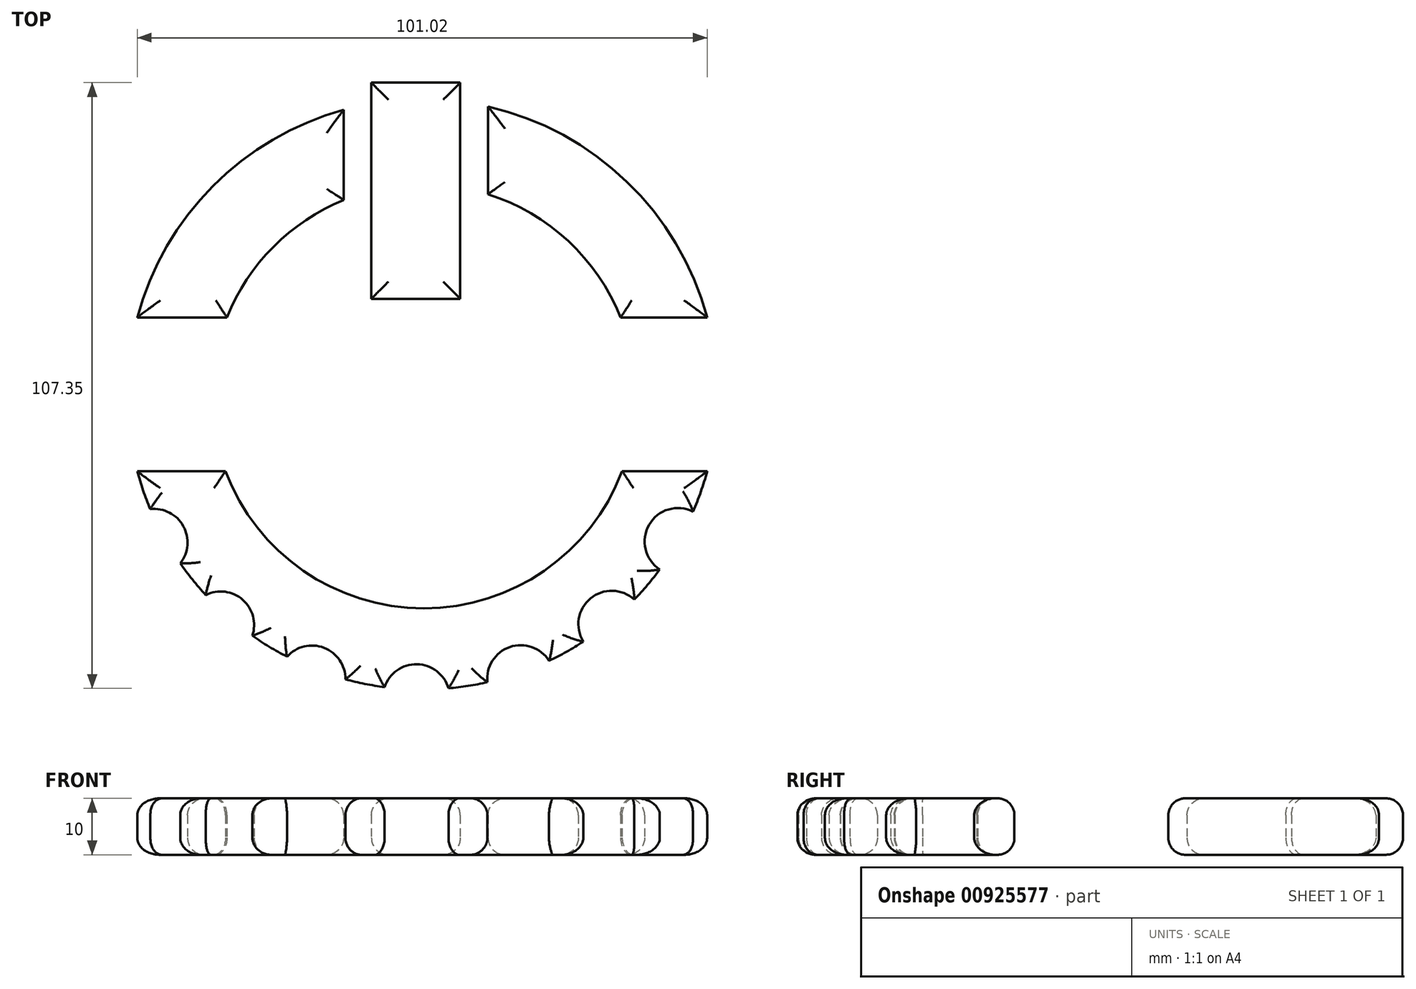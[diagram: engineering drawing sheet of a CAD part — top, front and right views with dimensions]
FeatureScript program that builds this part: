
annotation { "Feature Type Name" : "Feature", "Feature Type Description" : "" }
export const myFeature = defineFeature(function(context is Context, id is Id, definition is map)
    precondition{}
    {
        {
            var Q0;
            Q0=qCreatedBy(makeId("Top.planeOp"),FACE);
            var sketch = newSketch(context, id + "F0", { "sketchPlane" : qUnion([Q0])});
            skArc(sketch, "E0", {"start": v(-12.8, 35.35) * mm, "mid": v(-25.25, 27.04) * mm, "end": v(-33.48, 14.53) * mm});
            skArc(sketch, "E1", {"start": v(-12.8, 51.32) * mm, "mid": v(-35.97, 37.78) * mm, "end": v(-49.38, 14.53) * mm});
            skLineSegment(sketch, "E2.bottom", {"start": v(7.88, 17.84) * mm, "end": v(-7.88, 17.84) * mm});
            skLineSegment(sketch, "E2.top", {"start": v(7.88, 56.13) * mm, "end": v(-7.88, 56.13) * mm});
            skLineSegment(sketch, "E2.left", {"start": v(7.88, 17.84) * mm, "end": v(7.88, 56.13) * mm});
            skLineSegment(sketch, "E2.right", {"start": v(-7.88, 17.84) * mm, "end": v(-7.88, 56.13) * mm});
            skPoint(sketch, "E2.middle", {"position": v(0, 36.99) * mm});
            skLineSegment(sketch, "E3.bottom", {"start": v(51.64, -12.75) * mm, "end": v(36.57, -12.75) * mm});
            skLineSegment(sketch, "E3.top", {"start": v(51.64, 14.53) * mm, "end": v(36.3, 14.53) * mm});
            skArc(sketch, "E4", {"start": v(49.15, -19.89) * mm, "mid": v(41.35, -22.23) * mm, "end": v(43.25, -30.15) * mm});
            skPoint(sketch, "E5.orphan", {"position": v(12.8, 62.31) * mm});
            skPoint(sketch, "E6.orphan", {"position": v(-12.8, 61.71) * mm});
            skLineSegment(sketch, "E7.trimOffspring", {"start": v(12.8, 36.37) * mm, "end": v(12.8, 51.9) * mm});
            skLineSegment(sketch, "E8.trimOffspring", {"start": v(-12.8, 35.35) * mm, "end": v(-12.8, 51.32) * mm});
            skArc(sketch, "E9.trimOffspring", {"start": v(-49.38, -12.75) * mm, "mid": v(-48.34, -16.14) * mm, "end": v(-47.07, -19.46) * mm});
            skArc(sketch, "E10.trimOffspring", {"start": v(-33.75, -12.75) * mm, "mid": v(1.41, -37.04) * mm, "end": v(36.57, -12.75) * mm});
            skLineSegment(sketch, "E11.trimOffspring", {"start": v(-33.48, 14.53) * mm, "end": v(-49.38, 14.53) * mm});
            skPoint(sketch, "E3.right.end.orphan", {"position": v(-91.26, 14.53) * mm});
            skPoint(sketch, "E12.orphan", {"position": v(-55.52, -12.75) * mm});
            skLineSegment(sketch, "E13.trimOffspring", {"start": v(-33.75, -12.75) * mm, "end": v(-49.38, -12.75) * mm});
            skArc(sketch, "E14.trimOffspring", {"start": v(36.3, 14.53) * mm, "mid": v(27, 28.09) * mm, "end": v(12.8, 36.37) * mm});
            skPoint(sketch, "E15.left.start.orphan", {"position": v(12.8, 12.26) * mm});
            skPoint(sketch, "E15.right.start.orphan", {"position": v(-12.8, 11.66) * mm});
            skArc(sketch, "E16.trimOffspring", {"start": v(51.64, 14.53) * mm, "mid": v(37.4, 38.6) * mm, "end": v(12.8, 51.9) * mm});
            skPoint(sketch, "E17.orphan", {"position": v(93.52, -12.75) * mm});
            skArc(sketch, "E18.1.0", {"start": v(38.73, -35.48) * mm, "mid": v(30.97, -35.29) * mm, "end": v(29.68, -42.95) * mm});
            skArc(sketch, "E18.2.0", {"start": v(23.61, -46.35) * mm, "mid": v(16.65, -43.9) * mm, "end": v(12.7, -50.13) * mm});
            skArc(sketch, "E18.3.0", {"start": v(5.79, -51.22) * mm, "mid": v(0.2, -46.95) * mm, "end": v(-5.53, -51) * mm});
            skArc(sketch, "E18.4.0", {"start": v(-12.49, -49.62) * mm, "mid": v(-16.27, -44.03) * mm, "end": v(-22.83, -45.61) * mm});
            skArc(sketch, "E18.5.0", {"start": v(-28.98, -41.9) * mm, "mid": v(-30.7, -35.52) * mm, "end": v(-37.23, -34.68) * mm});
            skArc(sketch, "E18.6.0", {"start": v(-41.77, -29.05) * mm, "mid": v(-41.2, -22.48) * mm, "end": v(-47.07, -19.46) * mm});
            skPoint(sketch, "E18.center", {"position": v(0, 0) * mm});
            skLineSegment(sketch, "E18.anchor1", {"start": v(0, 0) * mm, "end": v(46.49, -25.18) * mm, "construction": true});
            skLineSegment(sketch, "E18.anchor2", {"start": v(0, 0) * mm, "end": v(-41.2, -22.5) * mm, "construction": true});
            skLineSegment(sketch, "E19.trimOffspring", {"start": v(-44.67, -24.4) * mm, "end": v(-46.4, -25.35) * mm, "construction": true});
            skArc(sketch, "E20.trimOffspring", {"start": v(-41.77, -29.05) * mm, "mid": v(-39.6, -31.94) * mm, "end": v(-37.23, -34.68) * mm});
            skArc(sketch, "E21.trimOffspring", {"start": v(-28.98, -41.9) * mm, "mid": v(-25.97, -43.86) * mm, "end": v(-22.83, -45.61) * mm});
            skArc(sketch, "E22.trimOffspring", {"start": v(-12.49, -49.62) * mm, "mid": v(-9.03, -50.43) * mm, "end": v(-5.53, -51) * mm});
            skArc(sketch, "E23.trimOffspring", {"start": v(5.79, -51.22) * mm, "mid": v(9.26, -50.79) * mm, "end": v(12.7, -50.13) * mm});
            skArc(sketch, "E24.trimOffspring", {"start": v(23.61, -46.35) * mm, "mid": v(26.7, -44.75) * mm, "end": v(29.68, -42.95) * mm});
            skArc(sketch, "E25.trimOffspring", {"start": v(38.73, -35.48) * mm, "mid": v(41.08, -32.9) * mm, "end": v(43.25, -30.15) * mm});
            skArc(sketch, "E26.trimOffspring", {"start": v(49.15, -19.89) * mm, "mid": v(50.52, -16.36) * mm, "end": v(51.64, -12.75) * mm});
            skSolve(sketch);
        }
        {
            var Q0;
            Q0 = qSketchRegion(id + "F0", true);
            extrude(context, id + "F1", {"entities" : qUnion([Q0]), "depth" : 10 * mm, "offsetDistance" : 25.4 * mm});
        }
        {
            var Q0;
            Q0=makeQuery(id+"F1.opExtrude","CAP_FACE",FACE,{"disambiguationData":[OSD([sQuery(id+"F0.wireOp",EDGE,"E3.bottom"),sQuery(id+"F0.wireOp",EDGE,"E4"),sQuery(id+"F0.wireOp",EDGE,"E9.trimOffspring"),sQuery(id+"F0.wireOp",EDGE,"E10.trimOffspring"),sQuery(id+"F0.wireOp",EDGE,"E13.trimOffspring"),sQuery(id+"F0.wireOp",EDGE,"E18.1.0"),sQuery(id+"F0.wireOp",EDGE,"E18.2.0"),sQuery(id+"F0.wireOp",EDGE,"E18.3.0"),sQuery(id+"F0.wireOp",EDGE,"E18.4.0"),sQuery(id+"F0.wireOp",EDGE,"E18.5.0"),sQuery(id+"F0.wireOp",EDGE,"E18.6.0"),sQuery(id+"F0.wireOp",EDGE,"E20.trimOffspring"),sQuery(id+"F0.wireOp",EDGE,"E21.trimOffspring"),sQuery(id+"F0.wireOp",EDGE,"E22.trimOffspring"),sQuery(id+"F0.wireOp",EDGE,"E23.trimOffspring"),sQuery(id+"F0.wireOp",EDGE,"E24.trimOffspring"),sQuery(id+"F0.wireOp",EDGE,"E25.trimOffspring"),sQuery(id+"F0.wireOp",EDGE,"E26.trimOffspring")])],"isStart":false});
            var Q1;
            Q1=makeQuery(id+"F1.opExtrude","CAP_FACE",FACE,{"disambiguationData":[OSD([sQuery(id+"F0.wireOp",EDGE,"E0"),sQuery(id+"F0.wireOp",EDGE,"E1"),sQuery(id+"F0.wireOp",EDGE,"E8.trimOffspring"),sQuery(id+"F0.wireOp",EDGE,"E11.trimOffspring")])],"isStart":false});
            var Q2;
            Q2=makeQuery(id+"F1.opExtrude","CAP_FACE",FACE,{"disambiguationData":[OSD([sQuery(id+"F0.wireOp",EDGE,"E2.bottom"),sQuery(id+"F0.wireOp",EDGE,"E2.top"),sQuery(id+"F0.wireOp",EDGE,"E2.left"),sQuery(id+"F0.wireOp",EDGE,"E2.right")])],"isStart":false});
            var Q3;
            Q3=makeQuery(id+"F1.opExtrude","CAP_FACE",FACE,{"disambiguationData":[OSD([sQuery(id+"F0.wireOp",EDGE,"E3.top"),sQuery(id+"F0.wireOp",EDGE,"E7.trimOffspring"),sQuery(id+"F0.wireOp",EDGE,"E14.trimOffspring"),sQuery(id+"F0.wireOp",EDGE,"E16.trimOffspring")])],"isStart":false});
            var Q4;
            Q4=makeQuery(id+"F1.opExtrude","CAP_EDGE",EDGE,{"disambiguationData":[OSD([sQuery(id+"F0.wireOp",EDGE,"E14.trimOffspring")])],"isStart":true});
            var Q5;
            Q5=makeQuery(id+"F1.opExtrude","CAP_FACE",FACE,{"disambiguationData":[OSD([sQuery(id+"F0.wireOp",EDGE,"E0"),sQuery(id+"F0.wireOp",EDGE,"E1"),sQuery(id+"F0.wireOp",EDGE,"E8.trimOffspring"),sQuery(id+"F0.wireOp",EDGE,"E11.trimOffspring")])],"isStart":true});
            var Q6;
            Q6=makeQuery(id+"F1.opExtrude","CAP_FACE",FACE,{"disambiguationData":[OSD([sQuery(id+"F0.wireOp",EDGE,"E3.bottom"),sQuery(id+"F0.wireOp",EDGE,"E4"),sQuery(id+"F0.wireOp",EDGE,"E9.trimOffspring"),sQuery(id+"F0.wireOp",EDGE,"E10.trimOffspring"),sQuery(id+"F0.wireOp",EDGE,"E13.trimOffspring"),sQuery(id+"F0.wireOp",EDGE,"E18.1.0"),sQuery(id+"F0.wireOp",EDGE,"E18.2.0"),sQuery(id+"F0.wireOp",EDGE,"E18.3.0"),sQuery(id+"F0.wireOp",EDGE,"E18.4.0"),sQuery(id+"F0.wireOp",EDGE,"E18.5.0"),sQuery(id+"F0.wireOp",EDGE,"E18.6.0"),sQuery(id+"F0.wireOp",EDGE,"E20.trimOffspring"),sQuery(id+"F0.wireOp",EDGE,"E21.trimOffspring"),sQuery(id+"F0.wireOp",EDGE,"E22.trimOffspring"),sQuery(id+"F0.wireOp",EDGE,"E23.trimOffspring"),sQuery(id+"F0.wireOp",EDGE,"E24.trimOffspring"),sQuery(id+"F0.wireOp",EDGE,"E25.trimOffspring"),sQuery(id+"F0.wireOp",EDGE,"E26.trimOffspring")])],"isStart":true});
            var Q7;
            Q7=makeQuery(id+"F1.opExtrude","CAP_FACE",FACE,{"disambiguationData":[OSD([sQuery(id+"F0.wireOp",EDGE,"E2.bottom"),sQuery(id+"F0.wireOp",EDGE,"E2.top"),sQuery(id+"F0.wireOp",EDGE,"E2.left"),sQuery(id+"F0.wireOp",EDGE,"E2.right")])],"isStart":true});
            var Q8;
            Q8=makeQuery(id+"F1.opExtrude","CAP_FACE",FACE,{"disambiguationData":[OSD([sQuery(id+"F0.wireOp",EDGE,"E3.top"),sQuery(id+"F0.wireOp",EDGE,"E7.trimOffspring"),sQuery(id+"F0.wireOp",EDGE,"E14.trimOffspring"),sQuery(id+"F0.wireOp",EDGE,"E16.trimOffspring")])],"isStart":true});
            fillet(context, id + "F2", {"entities" : qUnion([Q0, Q1, Q2, Q3, Q4, Q5, Q6, Q7, Q8]), "radius" : 3 * mm, "tangentPropagation" : true, "allowEdgeOverflow" : false});
        }
    });
